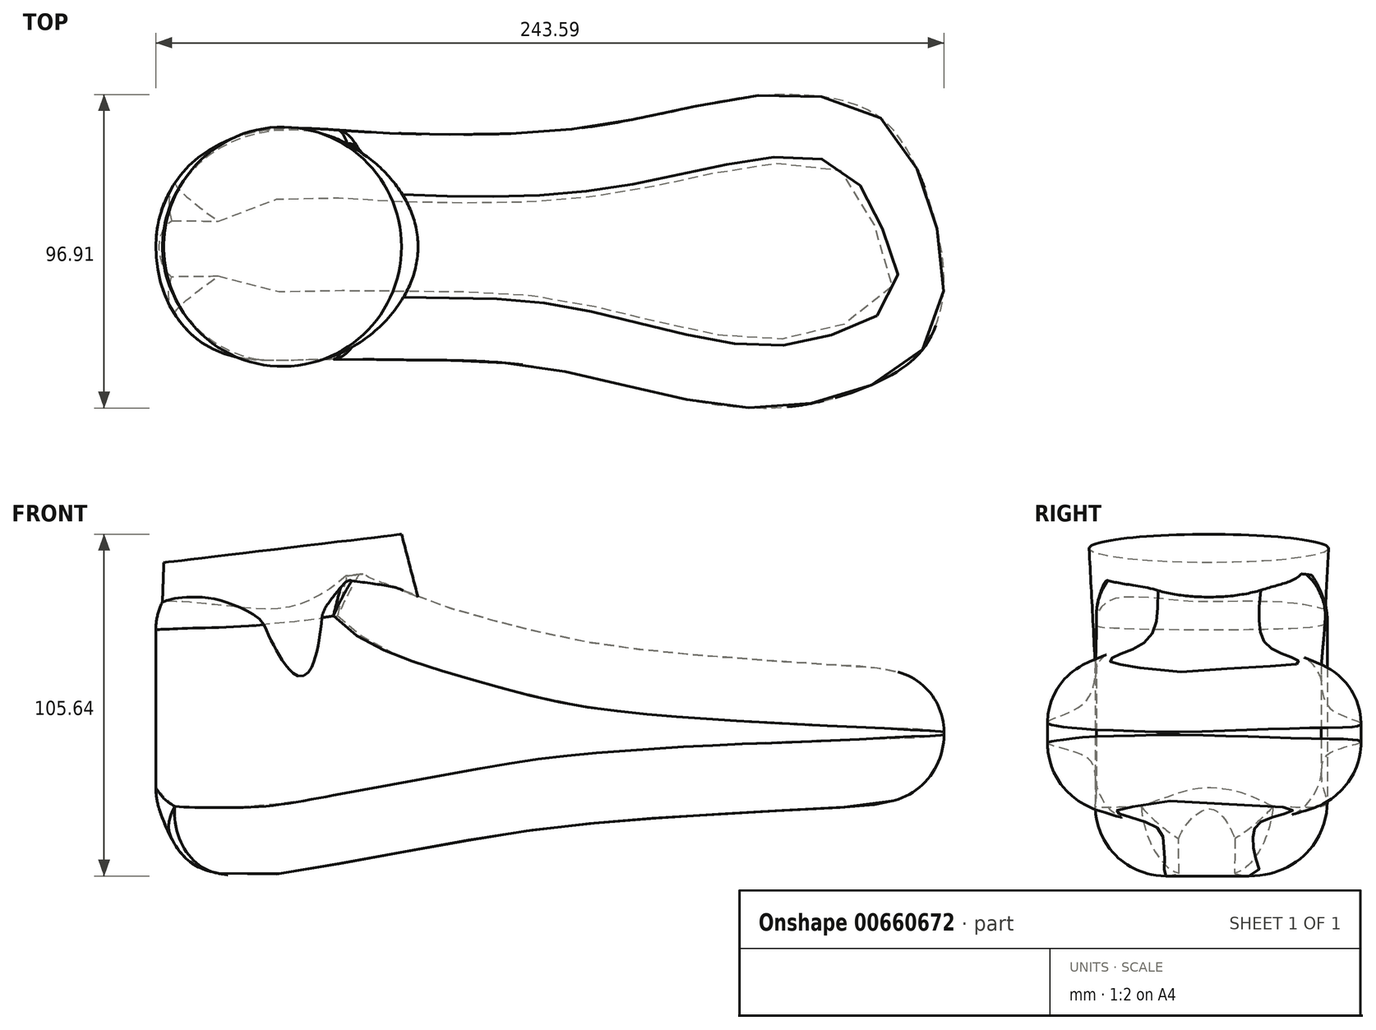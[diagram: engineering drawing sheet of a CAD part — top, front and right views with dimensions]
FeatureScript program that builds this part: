
annotation { "Feature Type Name" : "Feature", "Feature Type Description" : "" }
export const myFeature = defineFeature(function(context is Context, id is Id, definition is map)
    precondition{}
    {
        {
            var Q0;
            Q0=qCreatedBy(makeId("Top.planeOp"),FACE);
            cPlane(context, id + "F0", {"entities" : qUnion([Q0]), "cplaneType" : CPlaneType.OFFSET, "offset" : 10 * mm, "oppositeDirection" : true, "width" : 150 * mm, "height" : 150 * mm});
        }
        {
            var Q0;
            Q0=qCreatedBy(makeId("Front.planeOp"),FACE);
            var sketch = newSketch(context, id + "F1", { "sketchPlane" : qUnion([Q0])});
            skLineSegment(sketch, "E0", {"start": v(-126.2, 34.59) * mm, "end": v(0, 49.64) * mm, "construction": true});
            skSolve(sketch);
        }
        {
            var Q0;
            Q0=qCreatedBy(makeId("Right.planeOp"),FACE);
            var sketch = newSketch(context, id + "F2", { "sketchPlane" : qUnion([Q0])});
            skLineSegment(sketch, "E1.0", {"start": v(0, 34.59) * mm, "end": v(0, 49.64) * mm, "construction": true});
            skLineSegment(sketch, "E2", {"start": v(0, 49.64) * mm, "end": v(78.18, 49.64) * mm, "construction": true});
            skSolve(sketch);
        }
        {
            var Q0;
            Q0=sQuery(id+"F2.wireOp",VERTEX,"E2.end");
            var Q1;
            Q1=sQuery(id+"F2.wireOp",VERTEX,"E2.start");
            var Q2;
            Q2=sQuery(id+"F1.wireOp",VERTEX,"E0.start");
            cPlane(context, id + "F3", {"entities" : qUnion([Q0, Q1, Q2]), "cplaneType" : CPlaneType.THREE_POINT, "offset" : 25 * mm, "width" : 150 * mm, "height" : 150 * mm});
        }
        {
            var Q0;
            Q0=qCreatedBy(id+"F0.planeOp",FACE);
            cPlane(context, id + "F4", {"entities" : qUnion([Q0]), "cplaneType" : CPlaneType.OFFSET, "offset" : 70 * mm, "width" : 150 * mm, "height" : 150 * mm});
        }
        {
            var Q0;
            Q0=qCreatedBy(id+"F4.planeOp",FACE);
            var sketch = newSketch(context, id + "F5", { "sketchPlane" : qUnion([Q0])});
            skLineSegment(sketch, "E3.bottom", {"start": v(178, 87.04) * mm, "end": v(-168.77, 87.04) * mm});
            skLineSegment(sketch, "E3.top", {"start": v(178, -71.84) * mm, "end": v(-168.77, -71.84) * mm});
            skLineSegment(sketch, "E3.left", {"start": v(178, 87.04) * mm, "end": v(178, -71.84) * mm});
            skLineSegment(sketch, "E3.right", {"start": v(-168.77, 87.04) * mm, "end": v(-168.77, -71.84) * mm});
            skFitSpline(sketch, "E4", {"points": [v(112.25, -42.37) * mm, v(125.46, -31.4) * mm, v(130.92, -15.26) * mm, v(129.4, 3.7) * mm, v(122.2, 25.52) * mm, v(108.35, 43.13) * mm, v(82.74, 48.96) * mm, v(59.98, 47) * mm, v(19.69, 38.96) * mm, v(-18.8, 36.21) * mm, v(-55.07, 36.97) * mm, v(-78, 38.15) * mm, v(-97.37, 35.08) * mm, v(-113.72, 24.15) * mm, v(-122.11, 6.16) * mm, v(-120.89, -12.02) * mm, v(-115.3, -23.54) * mm, v(-105.57, -32.28) * mm, v(-91.66, -36.26) * mm, v(-71.4, -36.26) * mm, v(-39.4, -36.46) * mm, v(-2.44, -38.24) * mm, v(40.03, -47.42) * mm, v(79.93, -51.64) * mm, v(112.25, -42.37) * mm]});
            skSolve(sketch);
        }
        {
            var Q0;
            Q0=qCreatedBy(makeId("Front.planeOp"),FACE);
            var sketch = newSketch(context, id + "F6", { "sketchPlane" : qUnion([Q0])});
            skFitSpline(sketch, "E5", {"points": [v(-119.13, 38.44) * mm, v(-119.13, 33.94) * mm, v(-120.9, 4.27) * mm, v(-123.57, -25.48) * mm, v(-120.92, -39.45) * mm, v(-113.66, -52.87) * mm, v(-104.36, -58.06) * mm, v(-92.75, -59.32) * mm, v(-77.53, -57.75) * mm, v(-27.63, -48.8) * mm, v(12.86, -42.84) * mm, v(69.82, -38.75) * mm, v(100.89, -37.03) * mm, v(116.9, -34.52) * mm, v(127.68, -28.43) * mm, v(131.34, -21.72) * mm, v(132.41, -11.5) * mm, v(130.12, -3.1) * mm, v(121.42, 4.53) * mm, v(108.1, 7.85) * mm, v(96.18, 8.64) * mm, v(56.48, 11.46) * mm, v(17.18, 15.9) * mm, v(-17.61, 23.97) * mm, v(-45.56, 34.04) * mm, v(-53.77, 42.25) * mm, v(-55.62, 46.48) * mm, v(-60.65, 45.69) * mm, v(-113.57, 39.24) * mm, v(-119.13, 38.44) * mm]});
            skSolve(sketch);
        }
        {
            var Q0;
            Q0=qSketchRegion(id+"F6",true);
            extrude(context, id + "F7", {"entities" : qUnion([Q0]), "depth" : 140 * mm, "symmetric" : true});
        }
        {
            var Q0;
            Q0=makeQuery(id+"F5.imprint","IMPRINT",FACE,{"disambiguationData":[TD([[makeQuery(id+"F5.imprint","IMPRINT",EDGE,{"derivedFrom":sQuery(id+"F5.wireOp",EDGE,"E3.bottom")}),1.0]])]});
            extrude(context, id + "F8", {"entities" : qUnion([Q0]), "operationType" : NewBodyOperationType.REMOVE, "oppositeDirection" : true, "depth" : 130 * mm});
        }
        {
            var Q0;
            Q0=makeQuery(id+"F8.boolean.opBoolean","INTERSECT",EDGE,{"disambiguationData":[OD(1.0)],"derivedFrom":[makeQuery(id+"F7.opExtrude","SWEPT_FACE",FACE,{"disambiguationData":[OSD([sQuery(id+"F6.wireOp",EDGE,"E5")])]}),makeQuery(id+"F8.opExtrude","SWEPT_FACE",FACE,{"disambiguationData":[OSD([sQuery(id+"F5.wireOp",EDGE,"E4")])]})]});
            fillet(context, id + "F9", {"entities" : qUnion([Q0]), "radius" : 20 * mm, "allowEdgeOverflow" : false});
        }
        {
            var Q0;
            Q0=makeQuery(id+"F8.boolean.opBoolean","INTERSECT",EDGE,{"disambiguationData":[OD(0.0)],"derivedFrom":[makeQuery(id+"F7.opExtrude","SWEPT_FACE",FACE,{"disambiguationData":[OSD([sQuery(id+"F6.wireOp",EDGE,"E5")])]}),makeQuery(id+"F8.opExtrude","SWEPT_FACE",FACE,{"disambiguationData":[OSD([sQuery(id+"F5.wireOp",EDGE,"E4")])]})]});
            fillet(context, id + "F10", {"entities" : qUnion([Q0]), "radius" : 22 * mm, "tangentPropagation" : true, "allowEdgeOverflow" : false});
        }
        {
            var Q0;
            Q0=qCreatedBy(id+"F3.planeOp",FACE);
            var sketch = newSketch(context, id + "F11", { "sketchPlane" : qUnion([Q0])});
            skLineSegment(sketch, "E6.bottom", {"start": v(-167.37, -58.49) * mm, "end": v(31.87, -58.49) * mm});
            skLineSegment(sketch, "E6.top", {"start": v(-167.37, 81.96) * mm, "end": v(31.87, 81.96) * mm});
            skLineSegment(sketch, "E6.left", {"start": v(-167.37, -58.49) * mm, "end": v(-167.37, 81.96) * mm});
            skLineSegment(sketch, "E6.right", {"start": v(31.87, -58.49) * mm, "end": v(31.87, 81.96) * mm});
            skSolve(sketch);
        }
        {
            var Q0;
            Q0=makeQuery(id+"F11.imprint","IMPRINT",FACE,{"disambiguationData":[TD([[makeQuery(id+"F11.imprint","IMPRINT",EDGE,{"derivedFrom":sQuery(id+"F11.wireOp",EDGE,"E6.bottom")}),1.0]])]});
            extrude(context, id + "F12", {"entities" : qUnion([Q0]), "operationType" : NewBodyOperationType.REMOVE, "depth" : 10 * mm, "symmetric" : true});
        }
        {
            var Q0;
            Q0=makeQuery(id+"F7.opExtrude","SWEPT_BODY",BODY,{"disambiguationData":[OSD([sQuery(id+"F6.wireOp",EDGE,"E5")])]});
            var Q1;
            Q1=qCreatedBy(makeId("Origin.pointOp"),VERTEX);
            transform(context, id + "F13", {"entities" : qUnion([Q0]), "transformType" : TransformType.SCALE_UNIFORMLY, "scale" : 0.96, "scalePoint" : qUnion([Q1]), "makeCopy" : false});
        }
        {
            var Q0;
            Q0=qCreatedBy(id+"F3.planeOp",FACE);
            cPlane(context, id + "F14", {"entities" : qUnion([Q0]), "cplaneType" : CPlaneType.OFFSET, "offset" : 96 * mm, "oppositeDirection" : true, "width" : 150 * mm, "height" : 150 * mm});
        }
        {
            var Q0;
            Q0=qCreatedBy(id+"F14.planeOp",FACE);
            cPlane(context, id + "F15", {"entities" : qUnion([Q0]), "cplaneType" : CPlaneType.OFFSET, "offset" : 100 * mm, "width" : 150 * mm, "height" : 150 * mm});
        }
        {
            var Q0;
            Q0=qCreatedBy(id+"F15.planeOp",FACE);
            var sketch = newSketch(context, id + "F16", { "sketchPlane" : qUnion([Q0])});
            skCircle(sketch, "E7", {"center": v(-72.68, 0) * mm, "radius": 37 * mm});
            skSolve(sketch);
        }
        {
            var Q0;
            Q0=qCreatedBy(id+"F3.planeOp",FACE);
            cPlane(context, id + "F17", {"entities" : qUnion([Q0]), "cplaneType" : CPlaneType.OFFSET, "offset" : 45 * mm, "oppositeDirection" : true, "width" : 150 * mm, "height" : 150 * mm});
        }
        {
            var Q0;
            Q0=qCreatedBy(id+"F17.planeOp",FACE);
            var sketch = newSketch(context, id + "F18", { "sketchPlane" : qUnion([Q0])});
            skEllipse(sketch, "E8", {"center": v(-73.07, 0) * mm, "majorRadius": 44.16 * mm, "minorRadius": 34.46 * mm, "majorAxis": v(1, 0)});
            skSolve(sketch);
        }
        {
            var Q1;
            Q1=qSketchRegion(id+"F16",true);
            var Q2;
            Q2=qSketchRegion(id+"F18",true);
            loft(context, id + "F19", {"operationType" : NewBodyOperationType.ADD, "sheetProfilesArray" : [{ "sheetProfileEntities" : qUnion([Q1]) }, { "sheetProfileEntities" : qUnion([Q2]) }]});
        }
        {
            var Q0;
            Q0=qCreatedBy(makeId("Right.planeOp"),FACE);
            cPlane(context, id + "F20", {"entities" : qUnion([Q0]), "cplaneType" : CPlaneType.OFFSET, "offset" : 140 * mm, "width" : 150 * mm, "height" : 150 * mm});
        }
        {
            var Q0;
            Q0=qCreatedBy(makeId("Right.planeOp"),FACE);
            cPlane(context, id + "F21", {"entities" : qUnion([Q0]), "cplaneType" : CPlaneType.OFFSET, "offset" : 140 * mm, "oppositeDirection" : true, "width" : 150 * mm, "height" : 150 * mm});
        }
    });
